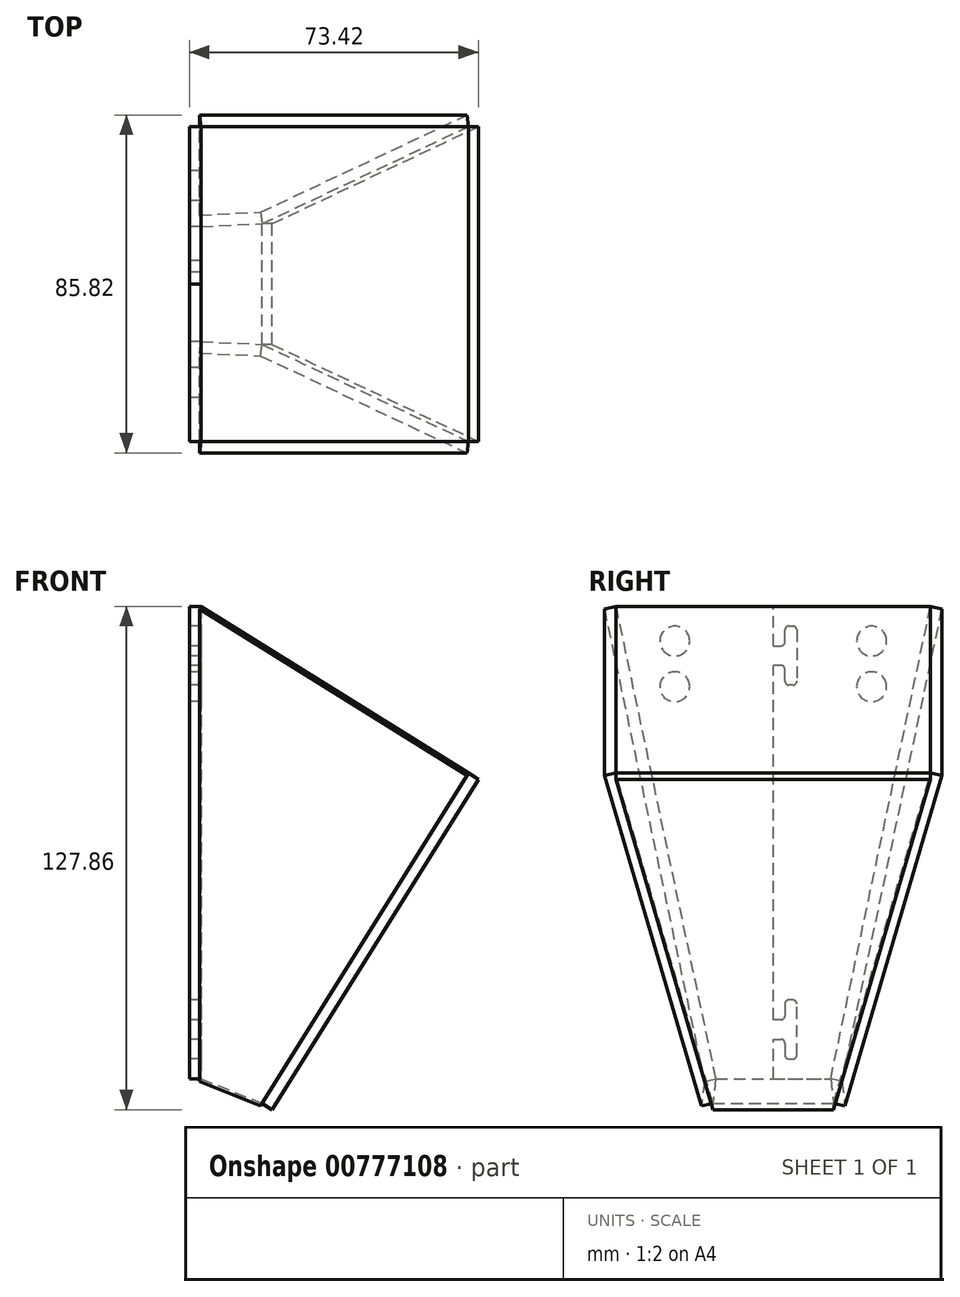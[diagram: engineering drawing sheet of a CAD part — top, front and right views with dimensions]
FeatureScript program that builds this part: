
annotation { "Feature Type Name" : "Feature", "Feature Type Description" : "" }
export const myFeature = defineFeature(function(context is Context, id is Id, definition is map)
    precondition{}
    {
        {
            assignVariable(context, id + "F0", {"name" : "pw", "anyValue" : 80});
        }
        {
            assignVariable(context, id + "F1", {"name" : "angle", "anyValue" : 14});
        }
        {
            assignVariable(context, id + "F2", {"name" : "wt", "anyValue" : 3});
        }
        {
            var Q0;
            Q0=qCreatedBy(makeId("Front.planeOp"),FACE);
            var sketch = newSketch(context, id + "F3", { "sketchPlane" : qUnion([Q0])});
            skLineSegment(sketch, "E0", {"start": v(0, 0) * mm, "end": v(0, -120) * mm});
            skLineSegment(sketch, "E1", {"start": v(0, -120) * mm, "end": v(15.51, -126.27) * mm});
            skLineSegment(sketch, "E2", {"start": v(15.51, -126.27) * mm, "end": v(67.87, -42.35) * mm});
            skLineSegment(sketch, "E3", {"start": v(67.87, -42.35) * mm, "end": v(0, 0) * mm});
            skSolve(sketch);
        }
        {
            var Q0;
            Q0=makeQuery(id+"F3.imprint","IMPRINT",FACE,{"disambiguationData":[TD([[makeQuery(id+"F3.imprint","IMPRINT",EDGE,{"derivedFrom":sQuery(id+"F3.wireOp",EDGE,"E0")}),1.0]])]});
            extrude(context, id + "F4", {"entities" : qUnion([Q0]), "endBound" : BoundingType.SYMMETRIC, "depth" : (getVariable(context, 'pw')) * mm, "offsetDistance" : 25 * mm});
        }
        {
            var Q0;
            Q0=makeQuery(id+"F4.opExtrude","CAP_EDGE",EDGE,{"disambiguationData":[OSD([sQuery(id+"F3.wireOp",EDGE,"E3")])],"isStart":true});
            cPlane(context, id + "F5", {"entities" : qUnion([Q0]), "cplaneType" : CPlaneType.LINE_ANGLE, "offset" : 25 * mm, "angle" : (getVariable(context, 'angle')) * degree, "width" : 150 * mm, "height" : 150 * mm});
        }
        {
            var Q0;
            Q0=qCreatedBy(id+"F5.planeOp",FACE);
            var sketch = newSketch(context, id + "F6", { "sketchPlane" : qUnion([Q0])});
            skLineSegment(sketch, "E4.0", {"start": v(5.01, 8.28) * mm, "end": v(8.2, -109.12) * mm});
            skLineSegment(sketch, "E5", {"start": v(5.01, 8.28) * mm, "end": v(91.84, 10.63) * mm});
            skLineSegment(sketch, "E6", {"start": v(91.84, 10.63) * mm, "end": v(95.85, -137.25) * mm});
            skLineSegment(sketch, "E7", {"start": v(95.85, -137.25) * mm, "end": v(5.01, -139.7) * mm});
            skLineSegment(sketch, "E8", {"start": v(5.01, -139.7) * mm, "end": v(5.01, 8.28) * mm});
            skSolve(sketch);
        }
        {
            var Q0;
            Q0=makeQuery(id+"F6.imprint","IMPRINT",FACE,{"disambiguationData":[TD([[makeQuery(id+"F6.imprint","IMPRINT",EDGE,{"derivedFrom":sQuery(id+"F6.wireOp",EDGE,"E5")}),-1.0]])]});
            extrude(context, id + "F7", {"entities" : qUnion([Q0]), "operationType" : NewBodyOperationType.REMOVE, "oppositeDirection" : true, "depth" : 50 * mm, "offsetDistance" : 25 * mm});
        }
        {
            var Q0;
            Q0=makeQuery(id+"F4.opExtrude","CAP_EDGE",EDGE,{"disambiguationData":[OSD([sQuery(id+"F3.wireOp",EDGE,"E3")])],"isStart":false});
            cPlane(context, id + "F8", {"entities" : qUnion([Q0]), "cplaneType" : CPlaneType.LINE_ANGLE, "offset" : 25 * mm, "angle" : (getVariable(context, 'angle')) * degree, "oppositeDirection" : true, "width" : 150 * mm, "height" : 150 * mm});
        }
        {
            var Q0;
            Q0=qCreatedBy(id+"F8.planeOp",FACE);
            var sketch = newSketch(context, id + "F9", { "sketchPlane" : qUnion([Q0])});
            skLineSegment(sketch, "E9", {"start": v(5.01, 8.28) * mm, "end": v(94.17, 9.57) * mm});
            skLineSegment(sketch, "E10", {"start": v(94.17, 9.57) * mm, "end": v(96.26, -134.3) * mm});
            skLineSegment(sketch, "E11", {"start": v(96.26, -134.3) * mm, "end": v(-8.54, -135.82) * mm});
            skLineSegment(sketch, "E12", {"start": v(5.01, 8.28) * mm, "end": v(-8.54, -135.82) * mm});
            skSolve(sketch);
        }
        {
            var Q0;
            Q0=makeQuery(id+"F9.imprint","IMPRINT",FACE,{"disambiguationData":[TD([[makeQuery(id+"F9.imprint","IMPRINT",EDGE,{"derivedFrom":sQuery(id+"F9.wireOp",EDGE,"E9")}),-1.0]])]});
            extrude(context, id + "F10", {"entities" : qUnion([Q0]), "operationType" : NewBodyOperationType.REMOVE, "depth" : 50 * mm, "offsetDistance" : 25 * mm});
        }
        {
            var Q0;
            Q0=makeQuery(id+"F7.boolean.opBoolean","COPY",FACE,{"derivedFrom":makeQuery(id+"F7.opExtrude","CAP_FACE",FACE,{"disambiguationData":[OSD([sQuery(id+"F6.wireOp",EDGE,"E5"),sQuery(id+"F6.wireOp",EDGE,"E6"),sQuery(id+"F6.wireOp",EDGE,"E7"),sQuery(id+"F6.wireOp",EDGE,"E8")])],"isStart":true})});
            extrude(context, id + "F11", {"entities" : qUnion([Q0]), "depth" : (getVariable(context, 'wt')) * mm, "offsetDistance" : 25 * mm});
        }
        {
            var Q0;
            Q0=makeQuery(id+"F4.opExtrude","SWEPT_FACE",FACE,{"disambiguationData":[OSD([sQuery(id+"F3.wireOp",EDGE,"E0")])]});
            extrude(context, id + "F12", {"entities" : qUnion([Q0]), "depth" : (getVariable(context, 'wt')) * mm, "offsetDistance" : 25 * mm});
        }
        {
            var Q0;
            Q0=makeQuery(id+"F10.boolean.opBoolean","COPY",FACE,{"derivedFrom":makeQuery(id+"F10.opExtrude","CAP_FACE",FACE,{"disambiguationData":[OSD([sQuery(id+"F9.wireOp",EDGE,"E9"),sQuery(id+"F9.wireOp",EDGE,"E10"),sQuery(id+"F9.wireOp",EDGE,"E11"),sQuery(id+"F9.wireOp",EDGE,"E12")])],"isStart":true})});
            extrude(context, id + "F13", {"entities" : qUnion([Q0]), "depth" : (getVariable(context, 'wt')) * mm, "offsetDistance" : 25 * mm});
        }
        {
            var Q0;
            Q0=makeQuery(id+"F4.opExtrude","SWEPT_FACE",FACE,{"disambiguationData":[OSD([sQuery(id+"F3.wireOp",EDGE,"E2")])]});
            extrude(context, id + "F14", {"entities" : qUnion([Q0]), "depth" : (getVariable(context, 'wt')) * mm, "offsetDistance" : 25 * mm});
        }
        {
            var Q0;
            Q0=makeQuery(id+"F12.opExtrude","CAP_FACE",FACE,{"disambiguationData":[OSD([sQuery(id+"F3.wireOp",EDGE,"E0")])],"isStart":false});
            var sketch = newSketch(context, id + "F15", { "sketchPlane" : qUnion([Q0])});
            skLineSegment(sketch, "E13", {"start": v(0, -120) * mm, "end": v(0, 0) * mm});
            skLineSegment(sketch, "E14", {"start": v(0, -10) * mm, "end": v(-2, -10) * mm});
            skLineSegment(sketch, "E15", {"start": v(-3, -9) * mm, "end": v(-3, -6) * mm});
            skLineSegment(sketch, "E16", {"start": v(-4, -5) * mm, "end": v(-5, -5) * mm});
            skLineSegment(sketch, "E17", {"start": v(-6, -6) * mm, "end": v(-6, -19) * mm});
            skLineSegment(sketch, "E18", {"start": v(-5, -20) * mm, "end": v(-4, -20) * mm});
            skLineSegment(sketch, "E19", {"start": v(-3, -19) * mm, "end": v(-3, -16) * mm});
            skLineSegment(sketch, "E20", {"start": v(-2, -15) * mm, "end": v(0, -15) * mm});
            skPoint(sketch, "E21.visualSharp", {"position": v(-6, -5) * mm});
            skArc(sketch, "E21.filletArc", {"start": v(-5, -5) * mm, "mid": v(-5.7, -5.3) * mm, "end": v(-6, -6) * mm});
            skPoint(sketch, "E22.visualSharp", {"position": v(-6, -20) * mm});
            skArc(sketch, "E22.filletArc", {"start": v(-6, -19) * mm, "mid": v(-5.7, -19.7) * mm, "end": v(-5, -20) * mm});
            skPoint(sketch, "E23.visualSharp", {"position": v(-3, -20) * mm});
            skArc(sketch, "E23.filletArc", {"start": v(-4, -20) * mm, "mid": v(-3.3, -19.7) * mm, "end": v(-3, -19) * mm});
            skPoint(sketch, "E24.visualSharp", {"position": v(-3, -5) * mm});
            skArc(sketch, "E24.filletArc", {"start": v(-3, -6) * mm, "mid": v(-3.3, -5.3) * mm, "end": v(-4, -5) * mm});
            skPoint(sketch, "E25.visualSharp", {"position": v(-3, -10) * mm});
            skArc(sketch, "E25.filletArc", {"start": v(-3, -9) * mm, "mid": v(-2.7, -9.7) * mm, "end": v(-2, -10) * mm});
            skPoint(sketch, "E26.visualSharp", {"position": v(-3, -15) * mm});
            skArc(sketch, "E26.filletArc", {"start": v(-2, -15) * mm, "mid": v(-2.7, -15.3) * mm, "end": v(-3, -16) * mm});
            skLineSegment(sketch, "E27", {"start": v(0, -60) * mm, "end": v(8.46, -60) * mm, "construction": true});
            skLineSegment(sketch, "E28.MirrorCS", {"start": v(-2, -105) * mm, "end": v(0, -105) * mm});
            skArc(sketch, "E29.MirrorCS", {"start": v(-2, -105) * mm, "mid": v(-2.7, -104.7) * mm, "end": v(-3, -104) * mm});
            skLineSegment(sketch, "E30.MirrorCS", {"start": v(-3, -101) * mm, "end": v(-3, -104) * mm});
            skArc(sketch, "E31.MirrorCS", {"start": v(-4, -100) * mm, "mid": v(-3.3, -100.3) * mm, "end": v(-3, -101) * mm});
            skLineSegment(sketch, "E32.MirrorCS", {"start": v(-5, -100) * mm, "end": v(-4, -100) * mm});
            skArc(sketch, "E33.MirrorCS", {"start": v(-6, -101) * mm, "mid": v(-5.7, -100.3) * mm, "end": v(-5, -100) * mm});
            skLineSegment(sketch, "E34.MirrorCS", {"start": v(-6, -114) * mm, "end": v(-6, -101) * mm});
            skArc(sketch, "E35.MirrorCS", {"start": v(-5, -115) * mm, "mid": v(-5.7, -114.7) * mm, "end": v(-6, -114) * mm});
            skLineSegment(sketch, "E36.MirrorCS", {"start": v(-4, -115) * mm, "end": v(-5, -115) * mm});
            skArc(sketch, "E37.MirrorCS", {"start": v(-3, -114) * mm, "mid": v(-3.3, -114.7) * mm, "end": v(-4, -115) * mm});
            skLineSegment(sketch, "E38.MirrorCS", {"start": v(-3, -111) * mm, "end": v(-3, -114) * mm});
            skArc(sketch, "E39.MirrorCS", {"start": v(-3, -111) * mm, "mid": v(-2.7, -110.3) * mm, "end": v(-2, -110) * mm});
            skLineSegment(sketch, "E40.MirrorCS", {"start": v(0, -110) * mm, "end": v(-2, -110) * mm});
            skCircle(sketch, "E41", {"center": v(-25, -8.8) * mm, "radius": 3.8 * mm});
            skCircle(sketch, "E42", {"center": v(-25, -20.4) * mm, "radius": 3.8 * mm});
            skCircle(sketch, "E43.MirrorC", {"center": v(25, -8.8) * mm, "radius": 3.8 * mm});
            skCircle(sketch, "E44.MirrorC", {"center": v(25, -20.4) * mm, "radius": 3.8 * mm});
            skSolve(sketch);
        }
        {
            var Q0;
            {var subQ0=sQuery(id+"F15.wireOp",EDGE,"E13");var subQ7=makeQuery(id+"F15.imprint","INTERSECT",VERTEX,{"derivedFrom":[subQ0,sQuery(id+"F15.wireOp",EDGE,"E28.MirrorCS")]});Q0=makeQuery(id+"F15.imprint","IMPRINT",FACE,{"disambiguationData":[TD([[makeQuery(id+"F15.imprint","IMPRINT",EDGE,{"disambiguationData":[TD([[subQ7,1.0]])],"derivedFrom":subQ0}),-1.0]])]});}
            var Q1;
            {var subQ1=sQuery(id+"F15.wireOp",EDGE,"E14");Q1=makeQuery(id+"F15.imprint","IMPRINT",FACE,{"disambiguationData":[TD([[makeQuery(id+"F15.imprint","IMPRINT",EDGE,{"derivedFrom":subQ1}),1.0]])]});}
            var Q2;
            {var subQ0=sQuery(id+"F15.wireOp",EDGE,"E28.MirrorCS");Q2=makeQuery(id+"F15.imprint","IMPRINT",FACE,{"disambiguationData":[TD([[makeQuery(id+"F15.imprint","IMPRINT",EDGE,{"derivedFrom":subQ0}),-1.0]])]});}
            extrude(context, id + "F16", {"entities" : qUnion([Q0, Q1, Q2]), "oppositeDirection" : true, "depth" : (getVariable(context, 'wt')) * mm, "offsetDistance" : 25 * mm});
        }
        {
            var Q0;
            {var subQ5=sQuery(id+"F15.wireOp",EDGE,"E14");Q0=makeQuery(id+"F15.imprint","IMPRINT",FACE,{"disambiguationData":[TD([[makeQuery(id+"F15.imprint","IMPRINT",EDGE,{"derivedFrom":subQ5}),-1.0]])]});}
            extrude(context, id + "F17", {"entities" : qUnion([Q0]), "oppositeDirection" : true, "depth" : (getVariable(context, 'wt')) * mm, "offsetDistance" : 25 * mm});
        }
    });
